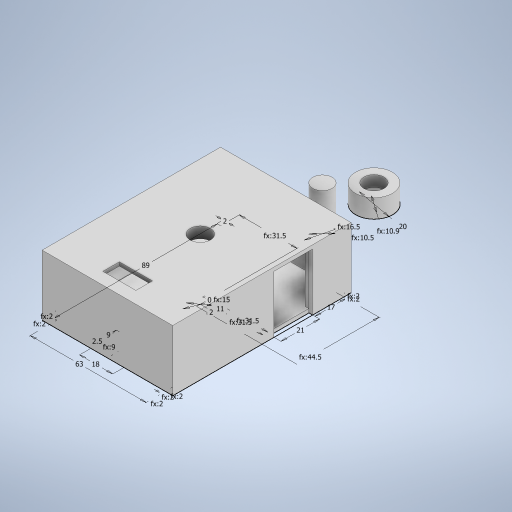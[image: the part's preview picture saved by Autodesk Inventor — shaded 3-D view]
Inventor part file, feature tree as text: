
AUTODESK INVENTOR PART (.ipt)
format: ipt  version: 2024 (Build 280153000, 153)  size: 364,544 bytes
history: native  units: mm
features: extrude x15, other x4
ambient origin geometry x8: Origin, YZ Plane, XZ Plane, XY Plane, X Axis, Y Axis, Z Axis, Center Point
bodies: Body1 (feature_tree), Body2 (feature_tree), Body3 (feature_tree)
feature tree (19):
  other  "Inside"
  other  "Bottom_sketch"
  extrude  "Bottom"  Depth=31.5mm
  extrude  "Side_Inside"  Depth=44.5mm
  extrude  "Side_Outside"  Depth=2.0mm
  extrude  "Top"  Depth=2.0mm
  extrude  "Lora_Hole"  Depth=2.0mm
  extrude  "TTL_Hole"  Depth=2.0mm TaperAngle=0.0deg
  extrude  "TTL_Outside"  TaperAngle=0.0deg  [1 undecoded]
  extrude  "Button_Hole"  Depth=2.0mm
  extrude  "Lora_Outside"  Depth=2.0mm
  extrude  "Button_slide"  Depth=2.0mm
  extrude  "TTL_Hole_v2"  Depth=2.0mm
  extrude  "Button_Piece"  Depth=31.0mm TaperAngle=0.0deg
  extrude  "Button_Bottom"  Depth=2.0mm TaperAngle=0.0deg
  extrude  "Button_Mushroom"  Depth=17.0mm
  extrude  "Mushroom_Inside"  Depth=29.0mm
  other  "Outside"
  other  "Button"
note: 1 required parameter value undecoded (feature->parameter linkage not recoverable at this tier; creation-order binding heuristic only, values carry confidence <= 0.55)
